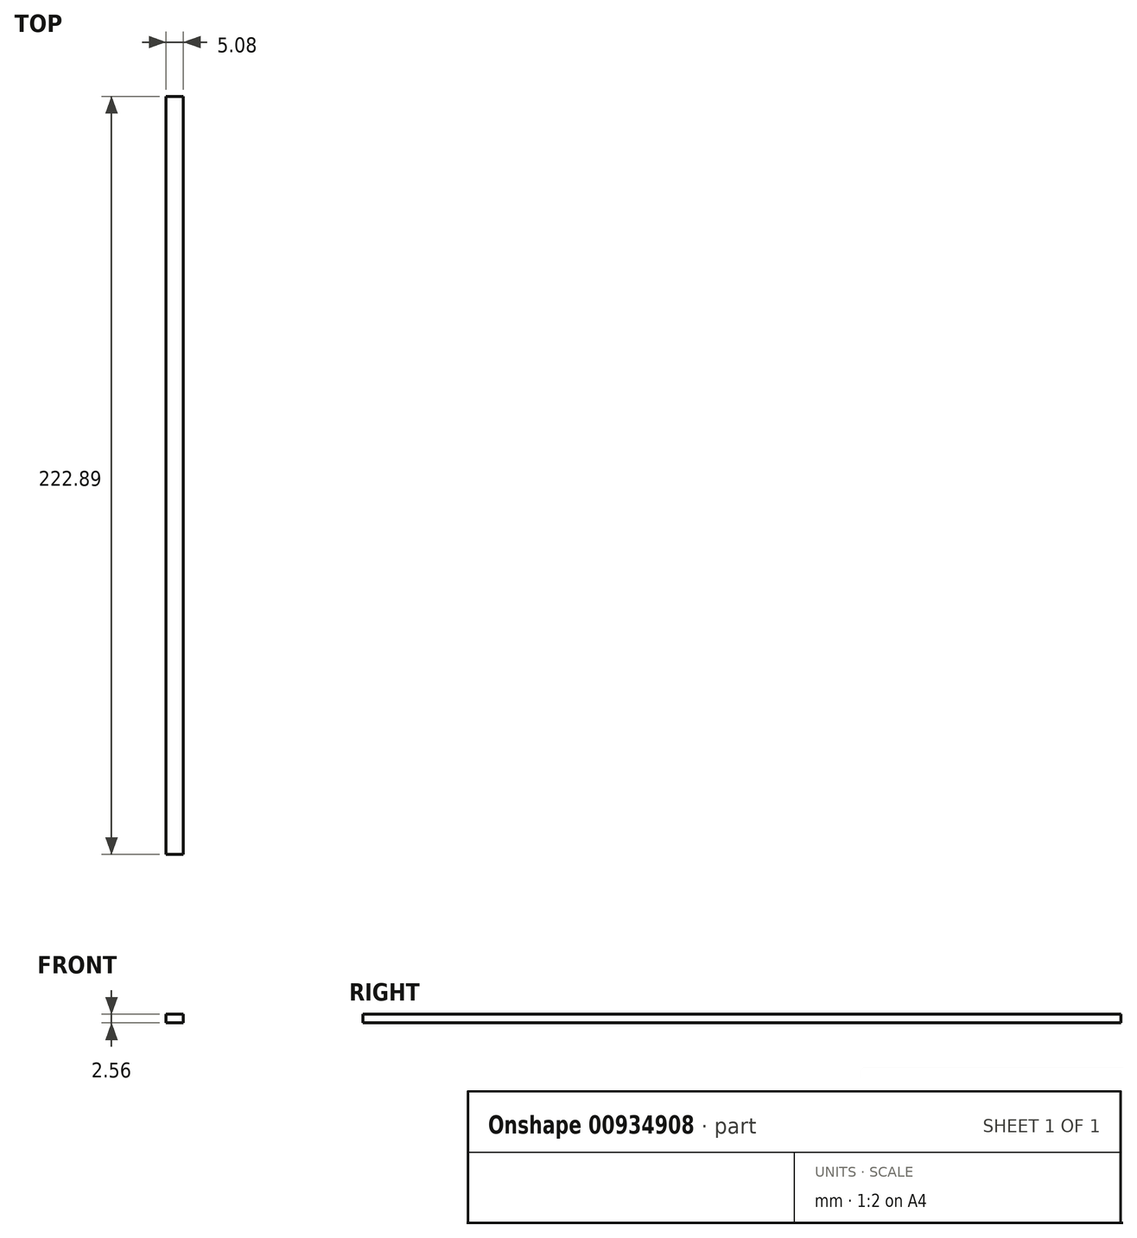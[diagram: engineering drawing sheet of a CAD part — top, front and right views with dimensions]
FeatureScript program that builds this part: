
annotation { "Feature Type Name" : "Feature", "Feature Type Description" : "" }
export const myFeature = defineFeature(function(context is Context, id is Id, definition is map)
    precondition{}
    {
        {
            var Q0;
            Q0=qCreatedBy(makeId("Right.planeOp"),FACE);
            var sketch = newSketch(context, id + "F0", { "sketchPlane" : qUnion([Q0])});
            skLineSegment(sketch, "E0.bottom", {"start": v(-73.22, 0) * mm, "end": v(149.67, 0) * mm});
            skLineSegment(sketch, "E0.top", {"start": v(-73.22, 2.56) * mm, "end": v(149.67, 2.56) * mm});
            skLineSegment(sketch, "E0.left", {"start": v(-73.22, 0) * mm, "end": v(-73.22, 2.56) * mm});
            skLineSegment(sketch, "E0.right", {"start": v(149.67, 0) * mm, "end": v(149.67, 2.56) * mm});
            skSolve(sketch);
        }
        {
            var Q0;
            Q0 = qSketchRegion(id + "F0", true);
            extrude(context, id + "F1", {"entities" : qUnion([Q0]), "depth" : 5.08 * mm, "offsetDistance" : 25.4 * mm});
        }
    });
